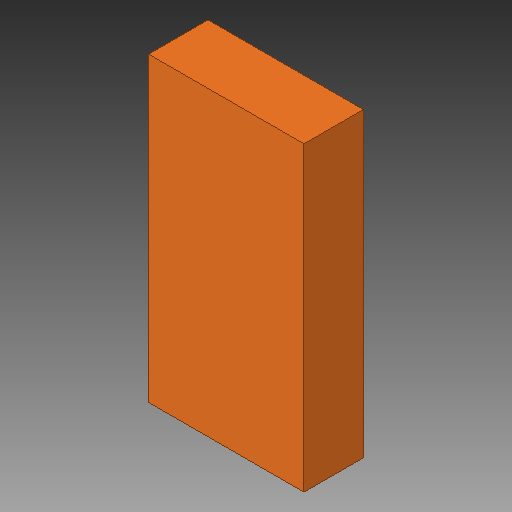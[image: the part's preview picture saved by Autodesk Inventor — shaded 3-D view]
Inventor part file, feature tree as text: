
AUTODESK INVENTOR PART (.ipt)
format: ipt  version: 2018 (Build 220112000, 112)  size: 79,872 bytes
history: native  units: in
note: dims shown in document units (in); Inventor stores cm internally (conversion verified against a paired STEP export)
features: other x1, extrude x1
ambient origin geometry x8: Origin, YZ Plane, XZ Plane, XY Plane, X Axis, Y Axis, Z Axis, Center Point
bodies: Solid1 (feature_tree)
feature tree (2):
  other  "JP1M, RTS_77"
  extrude  "Extrusion1"  Depth=0.0394in TaperAngle=0.0deg
